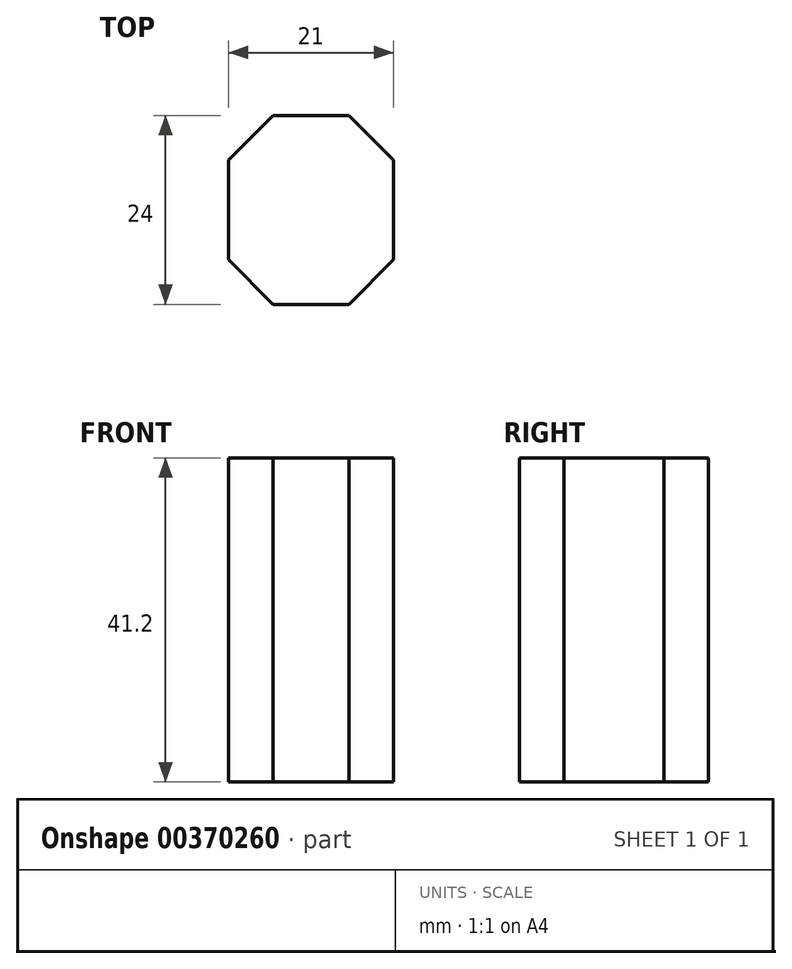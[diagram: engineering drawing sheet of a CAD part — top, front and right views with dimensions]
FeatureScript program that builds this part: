
annotation { "Feature Type Name" : "Feature", "Feature Type Description" : "" }
export const myFeature = defineFeature(function(context is Context, id is Id, definition is map)
    precondition{}
    {
        {
            var Q0;
            Q0=qCreatedBy(makeId("Top.planeOp"),FACE);
            var sketch = newSketch(context, id + "F0", { "sketchPlane" : qUnion([Q0])});
            skLineSegment(sketch, "E0.bottom", {"start": v(2.9, 9.65) * mm, "end": v(-6.8, 9.65) * mm});
            skLineSegment(sketch, "E0.top", {"start": v(2.9, -14.35) * mm, "end": v(-6.8, -14.35) * mm});
            skLineSegment(sketch, "E0.left", {"start": v(8.55, 4) * mm, "end": v(8.55, -8.7) * mm});
            skLineSegment(sketch, "E0.right", {"start": v(-12.45, 4) * mm, "end": v(-12.45, -8.7) * mm});
            skPoint(sketch, "E0.middle", {"position": v(-1.95, -2.35) * mm});
            skLineSegment(sketch, "E1", {"start": v(-6.8, 9.65) * mm, "end": v(-12.45, 4) * mm});
            skLineSegment(sketch, "E2", {"start": v(8.55, -8.7) * mm, "end": v(2.9, -14.35) * mm});
            skLineSegment(sketch, "E3", {"start": v(2.9, 9.65) * mm, "end": v(8.55, 4) * mm});
            skLineSegment(sketch, "E4", {"start": v(-12.45, -8.7) * mm, "end": v(-6.8, -14.35) * mm});
            skSolve(sketch);
        }
        {
            var Q0;
            Q0 = qSketchRegion(id + "F0", true);
            extrude(context, id + "F1", {"entities" : qUnion([Q0]), "depth" : 41.2 * mm});
        }
    });
